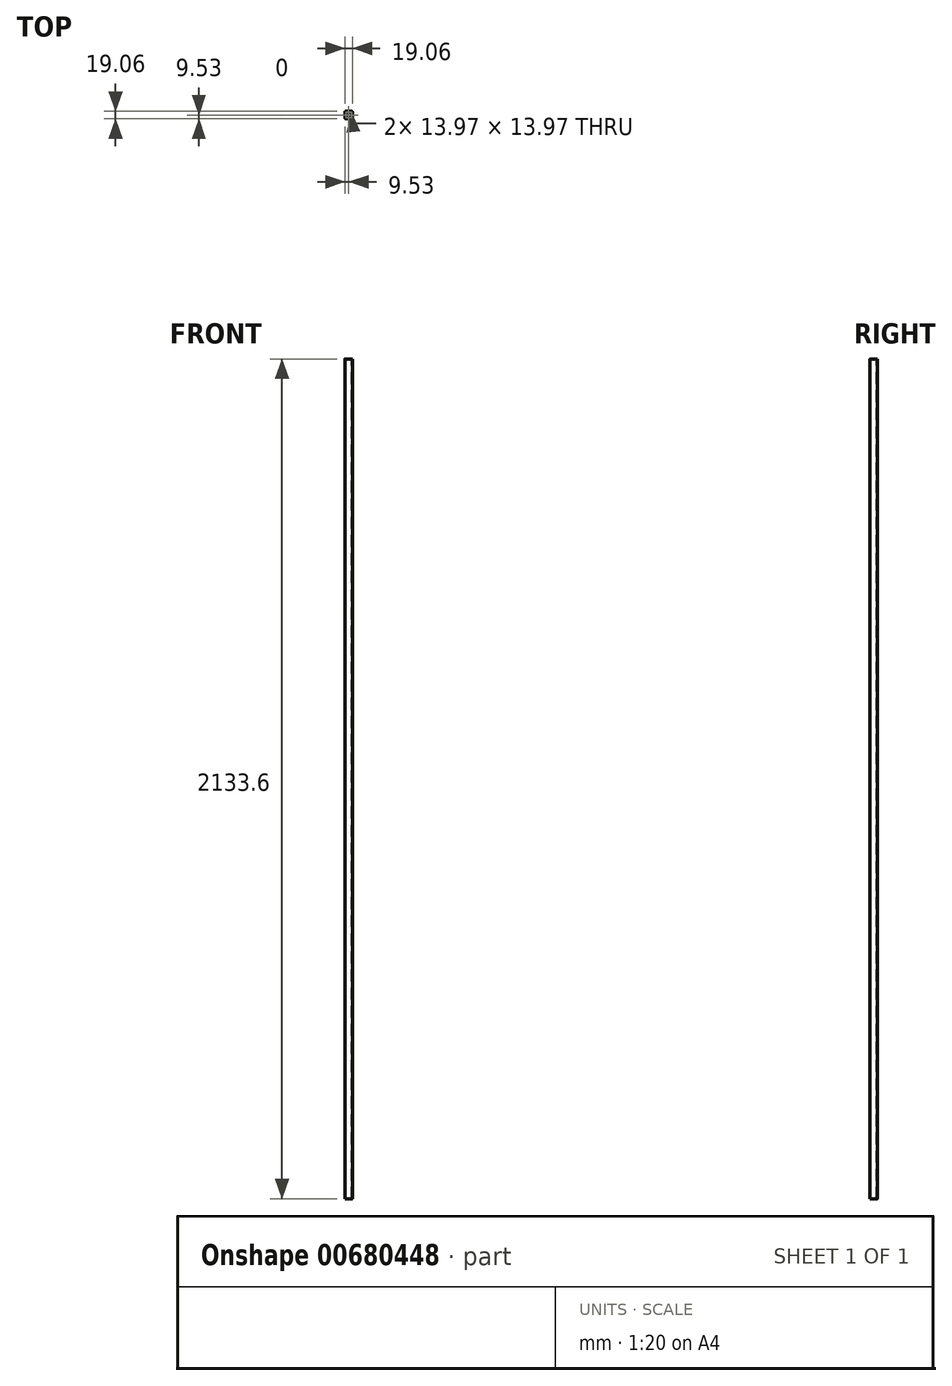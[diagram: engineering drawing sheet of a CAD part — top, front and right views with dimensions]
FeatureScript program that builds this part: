
annotation { "Feature Type Name" : "Feature", "Feature Type Description" : "" }
export const myFeature = defineFeature(function(context is Context, id is Id, definition is map)
    precondition{}
    {
        {
            var Q0;
            Q0=qCreatedBy(makeId("Top.planeOp"),FACE);
            var sketch = newSketch(context, id + "F0", { "sketchPlane" : qUnion([Q0])});
            skLineSegment(sketch, "E0.bottom", {"start": v(-9.53, -8.03) * mm, "end": v(-9.53, 8.02) * mm});
            skLineSegment(sketch, "E0.top", {"start": v(9.53, -8.03) * mm, "end": v(9.53, 8.02) * mm});
            skLineSegment(sketch, "E0.left", {"start": v(-8.03, -9.53) * mm, "end": v(8.03, -9.53) * mm});
            skLineSegment(sketch, "E0.right", {"start": v(-8.03, 9.52) * mm, "end": v(8.03, 9.52) * mm});
            skPoint(sketch, "E0.middle", {"position": v(0, 0) * mm});
            skPoint(sketch, "E1.visualSharp", {"position": v(-9.53, -9.53) * mm});
            skArc(sketch, "E1.filletArc", {"start": v(-9.53, -8.03) * mm, "mid": v(-9.09, -9.09) * mm, "end": v(-8.03, -9.53) * mm});
            skPoint(sketch, "E2.visualSharp", {"position": v(-9.53, 9.52) * mm});
            skArc(sketch, "E2.filletArc", {"start": v(-8.03, 9.52) * mm, "mid": v(-9.09, 9.09) * mm, "end": v(-9.53, 8.02) * mm});
            skPoint(sketch, "E3.visualSharp", {"position": v(9.53, 9.53) * mm});
            skArc(sketch, "E3.filletArc", {"start": v(9.53, 8.02) * mm, "mid": v(9.09, 9.09) * mm, "end": v(8.03, 9.52) * mm});
            skPoint(sketch, "E4.visualSharp", {"position": v(9.53, -9.53) * mm});
            skArc(sketch, "E4.filletArc", {"start": v(8.03, -9.53) * mm, "mid": v(9.09, -9.09) * mm, "end": v(9.53, -8.03) * mm});
            skLineSegment(sketch, "E5.0", {"start": v(-6.99, -6.99) * mm, "end": v(-6.99, 6.98) * mm});
            skLineSegment(sketch, "E5.1", {"start": v(-6.99, -6.99) * mm, "end": v(6.99, -6.99) * mm});
            skLineSegment(sketch, "E5.2", {"start": v(6.99, -6.99) * mm, "end": v(6.99, 6.98) * mm});
            skLineSegment(sketch, "E5.3", {"start": v(-6.99, 6.98) * mm, "end": v(6.99, 6.98) * mm});
            skSolve(sketch);
        }
        {
            var Q0;
            Q0=makeQuery(id+"F0.imprint","IMPRINT",FACE,{"disambiguationData":[TD([[makeQuery(id+"F0.imprint","IMPRINT",EDGE,{"derivedFrom":sQuery(id+"F0.wireOp",EDGE,"E0.bottom")}),-1.0]])]});
            extrude(context, id + "F1", {"entities" : qUnion([Q0]), "oppositeDirection" : true, "depth" : 13.5 * 152.4 * mm + 76.2 * mm, "offsetDistance" : 25 * mm});
        }
    });
